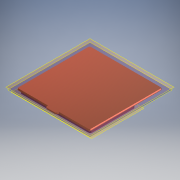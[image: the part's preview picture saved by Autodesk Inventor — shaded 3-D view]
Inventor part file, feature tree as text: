
AUTODESK INVENTOR PART (.ipt)
format: ipt  version: 2017 (Build 210142000, 142)  size: 444,928 bytes
history: native  units: mm
features: move_body x15, direct_edit x12, reference x11, sketch x7, extrude x6, other x5, plane x3, fillet x3, chamfer x1
ambient origin geometry x8: Origin, YZ Plane, XZ Plane, XY Plane, X Axis, Y Axis, Z Axis, Center Point
bodies: Solid1 (feature_tree)
feature tree (63):
  plane  "Work Plane1"
  extrude  "Extrusion1"  Depth=2.0mm
  sketch  "Sketch2"  dims[d3=5.5mm d4=2.0mm]
  plane  "Work Plane2"
  plane  "Work Plane3"
  extrude  "Extrusion2"  Depth=2.0mm
  extrude  "Extrusion3"  Depth=1.0mm
  extrude  "Extrusion4"  Depth=1.5mm TaperAngle=0.0deg
  extrude  "Extrusion5"  Depth=1.0mm TaperAngle=0.0deg
  fillet  "Fillet1"  Radius=1.75mm
  direct_edit  "Direct Edit1"
  fillet  "Fillet2"  Radius=1.0mm
  direct_edit  "Direct Edit2"
  direct_edit  "Direct Edit3"
  direct_edit  "Direct Edit4"
  direct_edit  "Direct Edit5"
  direct_edit  "Direct Edit6"
  direct_edit  "Direct Edit7"
  direct_edit  "Direct Edit8"
  direct_edit  "Direct Edit9"
  direct_edit  "Direct Edit10"
  chamfer  "Chamfer2"  Distance=15.5mm
  direct_edit  "Direct Edit11"
  sketch  "Sketch6"  dims[d23=2.0mm d24=0.0mm d25=0.0mm d26=15.5mm]
  direct_edit  "Direct Edit12"
  extrude  "Extrusion6"  Depth=0.5mm TaperAngle=0.0deg
  fillet  "Fillet3"  [1 undecoded]
  sketch  "Sketch1"  dims[d0=2.0mm d1=0.0mm d2=5.5mm]
  reference  "Reference2"
  sketch  "Sketch3"  dims[d5=1.0mm d6=0.0mm d7=1.0mm]
  reference  "Reference3"
  reference  "Reference4"
  reference  "Reference5"
  reference  "Reference6"
  reference  "Reference7"
  reference  "Reference8"
  reference  "Reference9"
  reference  "Reference10"
  reference  "Reference11"
  reference  "Reference12"
  sketch  "Sketch4"  dims[d8=100.0mm d10=7.62mm d11=10.0mm d13=10.0mm d15=1.5mm d16=0.0mm]
  sketch  "Sketch5"  dims[d17=1.5mm d18=3.75mm d19=0.0mm d20=1.75mm d21=0.0mm d22=1.0mm]
  sketch  "Sketch7"  dims[d27=0.0mm d28=0.0mm d29=-5.5mm d30=0.0mm d31=0.0mm d32=0.5mm d33=0.0mm d34=0.0mm d35=-4.0mm d36=0.0mm d37=0.0mm d38=2.5mm d39=0.0mm d40=0.0mm d41=-0.5mm d42=0.0mm d43=0.0mm d44=0.5mm d45=0.0mm d46=0.0mm d47=-0.5mm d48=0.0mm d49=0.0mm d50=-0.5mm d51=0.0mm d52=0.0mm d53=-0.5mm d57=0.0mm d58=0.0mm d59=-0.5mm d60=0.0mm d61=0.0mm d62=-0.9mm d63=0.0mm d64=0.0mm d65=-0.5mm d66=0.5mm d67=1.0mm d68=45.0deg d69=0.0mm d70=0.0mm d71=-13.0mm d72=0.0mm d73=0.0mm d74=0.6mm d75=13.0mm d76=6.0mm d77=1.5mm d78=0.0mm d79=2.0mm]
  parser-record x2  (decoder bookkeeping rows leaked as tree rows — omitted from the tree; the rows remain in map.json)
  other  "protoswitchboard.iam"
  other  "cover:1"
  other  "Delete1"
  move_body  "Move1"
  move_body  "Move2"
  move_body  "Move3"
  move_body  "Move4"
  move_body  "Move5"
  move_body  "Move6"
  move_body  "Move7"
  move_body  "Move8"
  move_body  "Move9"
  move_body  "Move10"
  move_body  "Move11"
  move_body  "Move12"
  move_body  "Move13"
  move_body  "Move14"
  move_body  "Move15"
note: 1 required parameter value undecoded (feature->parameter linkage not recoverable at this tier; creation-order binding heuristic only, values carry confidence <= 0.55)
note: 2 file-system paths scrubbed to <path> (originals preserved in map.json)
